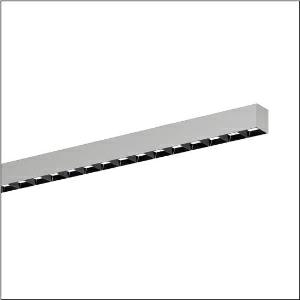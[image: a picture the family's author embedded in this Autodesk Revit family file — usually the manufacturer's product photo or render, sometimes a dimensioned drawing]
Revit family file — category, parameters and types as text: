
# Revit family: silica_r__21_51mx21tctas_c3b1
name_source: partatom
category: Lighting Fixtures
units: mm (PartAtom-declared; Revit-internal decimal feet)

## family parameters
Cut with Voids When Loaded = No
Host = Face
Light Source = No
Part Type = Normal
Room Calculation Point = No
Round Connector Dimension = Use Diameter
Shared = No

## types (1)
- --- (1 x LED, 9300 lm, 80.5 W, 6500K)
    Apparent Load = 81 VA
    CIE Flux Codes = 85 99 100 100 100
    Color Rendering = 80
    Color Temperature = 6500K
    Default Elevation = 1800 mm
    Description = Silica® 21, office luminaire, primary light control with darklight reflector, of PMMA, black, CAT 2 (L<= 3000cd/m²), light emission: direct distribution, primary light characteristic: symmetric, installation type: surface-mounted, LED, rated luminous flux: 9.300lm, luminous efficacy: 110lm/W, light colour: 8tw, colour temperature: 2700..6500K, control gear: ECG DALI, with terminal, 3+2-pole, max. 2.5mm², mains connection: 220..240V, AC, 50/60Hz, rated input power: 84.6W, luminaire housing, of aluminium, metallic grey (RAL 9006), length: 3.004mm, width: 53mm, height: 53mm, protection rating (complete): IP20, insulation class (complete): insulation class I (protective earthing), certification: CE, permissible operating ambient temperature: 0..+35°C, standard: EN 50419, packaging unit: 1 piece
    Height = 0 mm  [stored 0 ft]
    Lamp = 1 x LED
    Lamp Light Flux = 9300 lm
    Lamp Power = 80.5 W
    Lamp count = 1
    Length = 3004 mm
    Luminous efficacy = 116 lm/W
    Manufacturer = Siteco
    ModVariant = No
    Model = 51MX21TCTAS
    Mounting Place = Ceiling
    Mounting Type = Recessed
    Number of Poles = 1
    OnlyDefault = Yes
    Power Factor = 1
    Product Name = Silica® 21
    Product group = office luminaire | ceiling recessed
    ProductGroupID = 401
    Protection Class = Protection class I
    Protection Degree = IP 20
    RLX_Detail_Level = 1
    RLX_Emergency_Light_Flux = 0 lm
    RLX_Emergency_Type = 0
    RLX_Emergency_Type_DB = No
    RlxData = <blob elided: 60989 chars, md5=7184e7cd>
    Socket = socket
    Standby Power = 0 W
    System Light Flux = 9300 lm
    System Power = 81 W
    Type Comments = individual setting
    Type Image = l_1313585.jpg
    URL = http://relux.com
    VarID = @adj_089409
    Voltage = 0 V
    Weight = 0.00 kg
    Width = 53 mm

note: [stored X ft] marks values corroborated as IEEE doubles in the binary element streams (Revit-internal decimal feet)

## geometry (parser evidence)
native form markers: Blend x4, Sweep x11
no freeform markers — native parametric forms only
